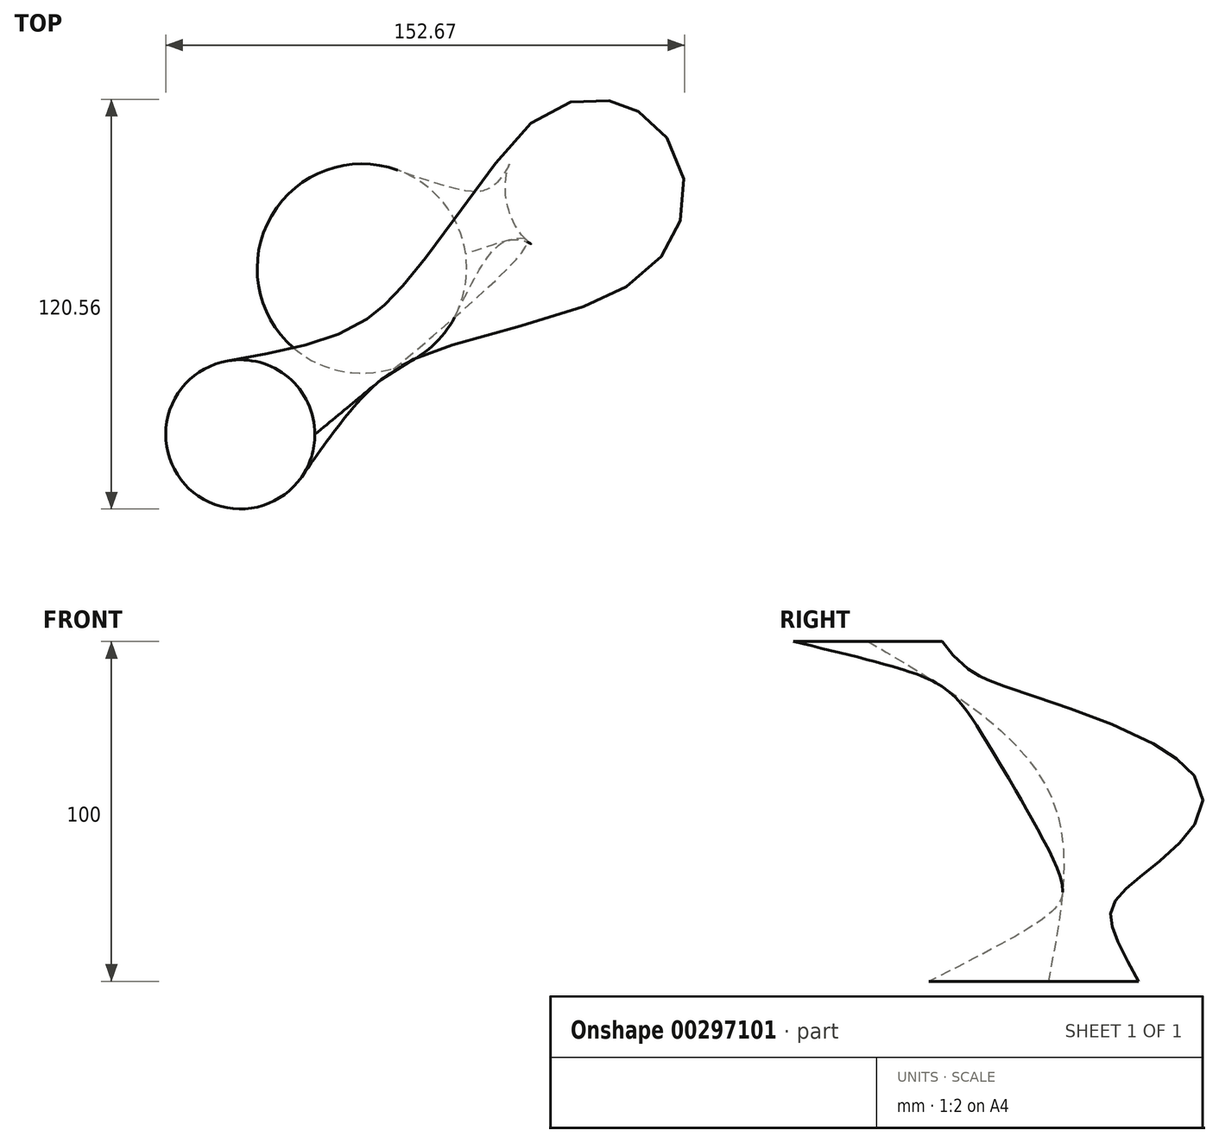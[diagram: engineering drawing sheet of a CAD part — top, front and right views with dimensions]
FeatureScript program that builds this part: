
annotation { "Feature Type Name" : "Feature", "Feature Type Description" : "" }
export const myFeature = defineFeature(function(context is Context, id is Id, definition is map)
    precondition{}
    {
        {
            var Q0;
            Q0=qCreatedBy(makeId("Top.planeOp"),FACE);
            var sketch = newSketch(context, id + "F0", { "sketchPlane" : qUnion([Q0])});
            skCircle(sketch, "E0", {"center": v(0, 0) * mm, "radius": 30.81 * mm});
            skSolve(sketch);
        }
        {
            var Q0;
            Q0=qCreatedBy(makeId("Top.planeOp"),FACE);
            cPlane(context, id + "F1", {"entities" : qUnion([Q0]), "cplaneType" : CPlaneType.OFFSET, "offset" : 50 * mm, "width" : 150 * mm, "height" : 150 * mm});
        }
        {
            var Q0;
            Q0=qCreatedBy(id+"F1.planeOp",FACE);
            var sketch = newSketch(context, id + "F2", { "sketchPlane" : qUnion([Q0])});
            skCircle(sketch, "E1", {"center": v(67.42, 23.73) * mm, "radius": 25.51 * mm});
            skSolve(sketch);
        }
        {
            var Q0;
            Q0=qCreatedBy(id+"F1.planeOp",FACE);
            cPlane(context, id + "F3", {"entities" : qUnion([Q0]), "cplaneType" : CPlaneType.OFFSET, "offset" : 50 * mm, "width" : 150 * mm, "height" : 150 * mm});
        }
        {
            var Q0;
            Q0=qCreatedBy(id+"F3.planeOp",FACE);
            var sketch = newSketch(context, id + "F4", { "sketchPlane" : qUnion([Q0])});
            skCircle(sketch, "E2", {"center": v(-35.77, -48.81) * mm, "radius": 21.95 * mm});
            skSolve(sketch);
        }
        {
            var Q0;
            Q0=makeQuery(id+"F4.imprint","IMPRINT",FACE,{"disambiguationData":[TD([[makeQuery(id+"F4.imprint","IMPRINT",EDGE,{"derivedFrom":sQuery(id+"F4.wireOp",EDGE,"E2")}),1.0]])]});
            var Q1;
            Q1=makeQuery(id+"F2.imprint","IMPRINT",FACE,{"disambiguationData":[TD([[makeQuery(id+"F2.imprint","IMPRINT",EDGE,{"derivedFrom":sQuery(id+"F2.wireOp",EDGE,"E1")}),1.0]])]});
            var Q2;
            Q2=makeQuery(id+"F0.imprint","IMPRINT",FACE,{"disambiguationData":[TD([[makeQuery(id+"F0.imprint","IMPRINT",EDGE,{"derivedFrom":sQuery(id+"F0.wireOp",EDGE,"E0")}),1.0]])]});
            loft(context, id + "F5", {"sheetProfilesArray" : [{ "sheetProfileEntities" : qUnion([Q0]) }, { "sheetProfileEntities" : qUnion([Q1]) }, { "sheetProfileEntities" : qUnion([Q2]) }]});
        }
    });
